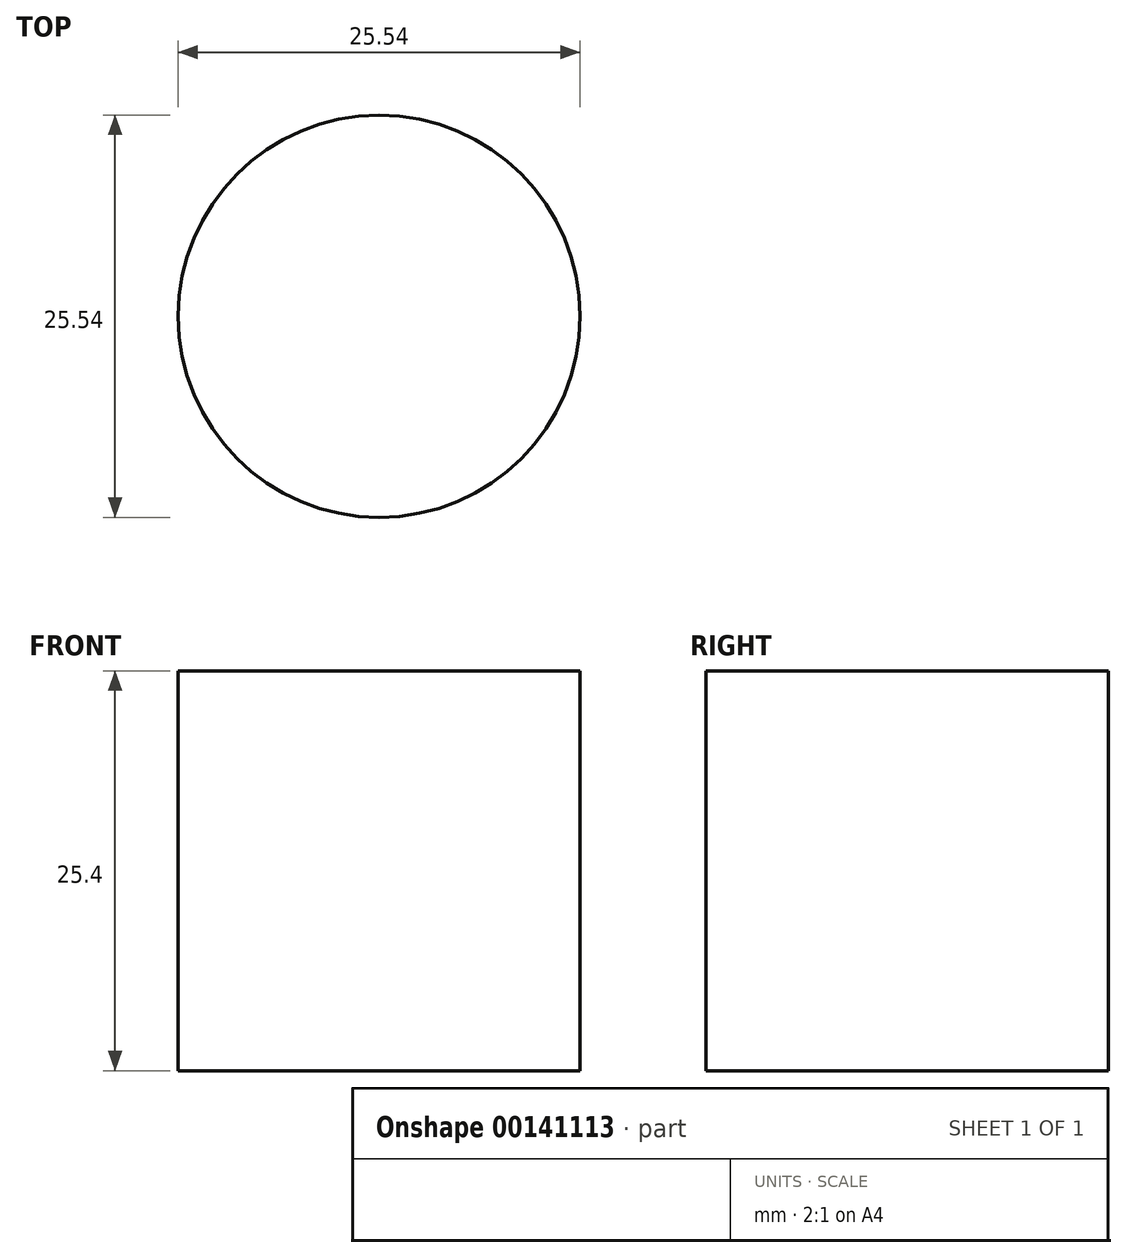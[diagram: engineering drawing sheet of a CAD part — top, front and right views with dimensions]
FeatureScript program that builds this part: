
annotation { "Feature Type Name" : "Feature", "Feature Type Description" : "" }
export const myFeature = defineFeature(function(context is Context, id is Id, definition is map)
    precondition{}
    {
        {
            var Q0;
            Q0=qCreatedBy(makeId("Top.planeOp"),FACE);
            var sketch = newSketch(context, id + "F0", { "sketchPlane" : qUnion([Q0])});
            skCircle(sketch, "E0", {"center": v(-57.04, -64.26) * mm, "radius": 12.77 * mm});
            skLineSegment(sketch, "E1", {"start": v(-44.3, -65.1) * mm, "end": v(-8.58, -65.1) * mm});
            skSolve(sketch);
        }
        {
            var Q0;
            Q0=makeQuery(id+"F0.imprint","IMPRINT",FACE,{"disambiguationData":[TD([[makeQuery(id+"F0.imprint","IMPRINT",EDGE,{"derivedFrom":sQuery(id+"F0.wireOp",EDGE,"E0")}),1.0]])]});
            var Q1;
            Q1=sQuery(id+"F0.wireOp",EDGE,"E0");
            extrude(context, id + "F1", {"entities" : qUnion([Q0]), "surfaceEntities" : qUnion([Q1]), "endBound" : BoundingType.SYMMETRIC, "depth" : 25.4 * mm});
        }
    });
